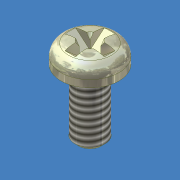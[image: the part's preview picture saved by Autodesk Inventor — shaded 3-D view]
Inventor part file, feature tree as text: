
AUTODESK INVENTOR PART (.ipt)
format: ipt  version: unknown  size: 269,824 bytes
history: native  units: mm (DEFAULTED — no unit token found)
features: other x29, sketch x4, extrude x3, revolve x1, thread x1, chamfer x1
ambient origin geometry x8: Origin, YZ Plane, XZ Plane, XY Plane, X Axis, Y Axis, Z Axis, Center Point
bodies: Solid1 (feature_tree)
feature tree (39):
  other  "Table"
  other  "Size = 2-56 UNC"
  other  "Length = 0.188"
  other  "Length = 0.375"
  other  "Length = 0.438"
  other  "Length = 0.625"
  other  "Length = 0.875"
  other  "Size = 4-40 UNC"
  other  "Length = 0.125"
  other  "Length = 0.313"
  other  "Size = 5-40 UNC"
  other  "Size = 6-32 UNC"
  other  "Size = 8-32 UNC"
  other  "Size = 10-24 UNC"
  other  "Size = 10-32 UNF"
  other  "Size = 1/4-20 UNC"
  other  "Size = 5/16-18 UNC"
  other  "Size = 3/8-16 UNC"
  other  "Length = 0.25"
  other  "Length = 0.75"
  other  "Length = 1"
  other  "Length = 0.5"
  other  "Length = 1.25"
  other  "Length = 1.5"
  other  "Length = 1.75"
  other  "Length = 2"
  other  "Length = 4"
  other  "Length = 2.5"
  other  "Length = 3"
  revolve  "Revolution1"  [1 undecoded]
  extrude  "Extrusion1"  Depth=2.1209mm
  extrude  "Extrusion2"  Depth=1.52908mm
  extrude  "Extrusion3"  Depth=1.3462mm
  thread  "Thread1"  [1 undecoded]
  chamfer  "Chamfer1"  Distance=0.7874mm
  sketch  "Sketch1"  dims[d0=2.1844mm d1=4.2418mm]
  sketch  "Sketch2"  dims[d2=0.889mm d3=2.1209mm]
  sketch  "Sketch3"  dims[d4=4.7752mm d6=1.52908mm]
  sketch  "Sketch4"  dims[d7=90.0deg d8=1.3462mm d9=3.18135mm d10=0.7874mm d11=0.0mm d12=3.18135mm d13=0.7874mm d14=0.0mm d15=0.76454mm d16=-5.235988mm d17=1.52908mm d18=4.5466mm d19=0.0mm d20=0.27305mm d21=0.27305mm d22=1.3462mm d23=45.0deg]
note: 2 required parameter values undecoded (feature->parameter linkage not recoverable at this tier; creation-order binding heuristic only, values carry confidence <= 0.55)